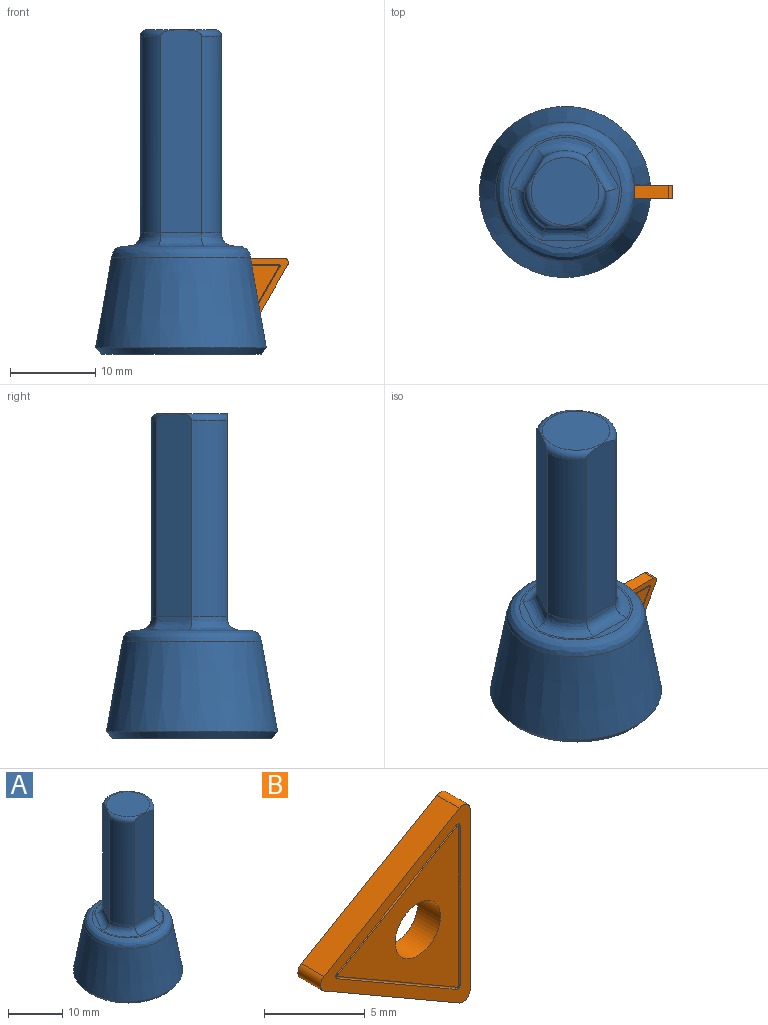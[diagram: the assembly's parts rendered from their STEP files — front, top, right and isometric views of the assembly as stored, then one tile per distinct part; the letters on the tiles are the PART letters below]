
ASSEMBLY  parts=2 mates=1
PART A: 28 faces, bbox 20.1x20.1x38.1 mm
  f0: plane 1.59x0.79mm, normal (0,0,-1), area 1mm2, adj f22,f27
  f1: cylinder r=4.76mm len=23.02mm, axis (0,0,-1), area 114.8mm2, adj f2,f6,f7,f15
  f2: plane 23.8x4.76mm, normal (0,-1,0), area 112.7mm2, adj f1,f3,f7,f13
  f3: cylinder r=4.76mm len=23.02mm, axis (0,0,-1), area 114.8mm2, adj f2,f4,f7,f14
  f4: plane 23.8x4.12mm, normal (0.87,0.5,0), area 112.7mm2, adj f3,f5,f7,f16
  f5: cylinder r=4.76mm len=23.02mm, axis (0,0,-1), area 114.8mm2, adj f4,f6,f7,f18
  f6: plane 23.8x4.12mm, normal (-0.87,0.5,0), area 112.7mm2, adj f1,f5,f7,f17
  f7: torus R=3.97mm, axis (0,0,1), area 22.8mm2, adj f1,f2,f3,f4,f5,f6,f8
  f8: plane 7.94x7.94mm, normal (0,0,1), area 49.5mm2, adj f7
  f9: plane 13.22x13.22mm, normal (0,0,1), area 17.5mm2, adj f13,f14,f15,f16,f17,f18,f19
  f10: cone r=7.94mm half-angle=10deg, axis (0,0,-1), area 598.1mm2, adj f11,f19,f20,f24,f26
  f11: cone r=7.94mm half-angle=10deg, axis (0,0,-1), area 0.9mm2, adj f10,f20,f25
  f12: plane 18.77x18.77mm, normal (0,0,-1), area 116.3mm2, adj f20,f21
  f13: bspline ~5.98x1.59mm, area 13.3mm2, adj f2,f9,f14,f15
  f14: bspline ~6.58x4.53mm, area 15.4mm2, adj f3,f9,f13,f16
  f15: bspline ~6.58x4.53mm, area 15.4mm2, adj f1,f9,f13,f17
  f16: bspline ~5.97x4.36mm, area 13.3mm2, adj f4,f9,f14,f18
  f17: bspline ~5.97x4.36mm, area 13.3mm2, adj f6,f9,f15,f18
  f18: bspline ~7.12x2.41mm, area 15.4mm2, adj f5,f9,f16,f17
  f19: bspline ~16.33x16.32mm, area 107.6mm2, adj f9,f10
  f20: cone r=10.04mm half-angle=40deg, axis (0,0,1), area 62.3mm2, adj f10,f11,f12,f23
  f21: cylinder r=7.14mm len=14.29mm, axis (0,0,-1), area 5.1mm2, adj f12,f22
  f22: cone r=0.79mm half-angle=30deg, axis (0,0,-1), area 297.3mm2, adj f0,f21,f23,f24,f25
  f23: plane 3.33x1.59mm, normal (0,0,1), area 5.2mm2, adj f20,f22,f24,f25
  f24: plane 10.51x10.03mm, normal (0,1,0), area 57.5mm2, adj f10,f22,f23,f26,f27
  f25: plane 10.51x10.03mm, normal (0,-1,0), area 57.5mm2, adj f11,f22,f23,f26,f27
  f26: plane 8.19x1.59mm, normal (0,0,-1), area 13mm2, adj f10,f24,f25,f27
  f27: plane 1.59x0.16mm, normal (1,0,0), area 0.2mm2, adj f0,f24,f25,f26
PART B: 23 faces, bbox 10.5x1.7x12 mm
  f0: plane 11.96x10.49mm, normal (0,1,0), area 23.6mm2, adj f2,f3,f4,f5,f6,f7,f15,f16
  f1: plane 11.96x10.49mm, normal (0,-1,0), area 23.6mm2, adj f2,f3,f4,f5,f6,f7,f8,f9
  f2: plane 10.94x1.57mm, normal (1,0,0), area 17.2mm2, adj f0,f1,f5,f7
  f3: plane 9.47x5.47mm, normal (-0.5,0,0.87), area 17.2mm2, adj f0,f1,f5,f6
  f4: plane 9.47x5.47mm, normal (-0.5,0,-0.87), area 17.2mm2, adj f0,f1,f6,f7
  f5: cylinder r=0.51mm len=1.57mm, axis (0,1,0), area 1.7mm2, adj f0,f1,f2,f3
  f6: cylinder r=0.51mm len=1.57mm, axis (0,1,0), area 1.7mm2, adj f0,f1,f3,f4
  f7: cylinder r=0.51mm len=1.57mm, axis (0,1,0), area 1.7mm2, adj f0,f1,f2,f4
  f8: cylinder r=0.06mm len=8.4mm, axis (-0.87,0,0.5), area 1.9mm2, adj f1,f9,f13,f14
  f9: torus R=0.13mm, axis (0,1,0), area 0.1mm2, adj f1,f8,f10,f14
  f10: cylinder r=0.06mm len=9.62mm, axis (0,0,-1), area 1.9mm2, adj f1,f9,f11,f14
  f11: torus R=0.13mm, axis (0,1,0), area 0.1mm2, adj f1,f10,f12,f14
  f12: cylinder r=0.06mm len=8.4mm, axis (0.87,0,0.5), area 1.9mm2, adj f1,f11,f13,f14
  f13: torus R=0.13mm, axis (0,1,0), area 0.1mm2, adj f1,f8,f12,f14
  f14: plane 9.75x8.46mm, normal (0,-1,0), area 34mm2, adj f8,f9,f10,f11,f12,f13,f22
  f15: cylinder r=0.06mm len=8.4mm, axis (-0.87,0,0.5), area 1.9mm2, adj f0,f16,f20,f21
  f16: torus R=0.13mm, axis (0,-1,0), area 0.1mm2, adj f0,f15,f17,f21
  f17: cylinder r=0.06mm len=9.62mm, axis (0,0,-1), area 1.9mm2, adj f0,f16,f18,f21
  f18: torus R=0.13mm, axis (0,-1,0), area 0.1mm2, adj f0,f17,f19,f21
  f19: cylinder r=0.06mm len=8.4mm, axis (0.87,0,0.5), area 1.9mm2, adj f0,f18,f20,f21
  f20: torus R=0.13mm, axis (0,-1,0), area 0.1mm2, adj f0,f15,f19,f21
  f21: plane 9.75x8.46mm, normal (0,1,0), area 34mm2, adj f15,f16,f17,f18,f19,f20,f22
  f22: cylinder r=1.59mm len=3.18mm, axis (0,1,0), area 15.7mm2, adj f14,f21
PLACE A t=(-15.24,-8.58,3.14)mm
PLACE B rot(axis=(0.26,0,-0.97),180deg) t=(-8.62,-8.58,-1.96)mm
MATE planar B.f3 <-> A.f26  axis (0,0,1) through (-8.62,-8.58,1.71)mm
